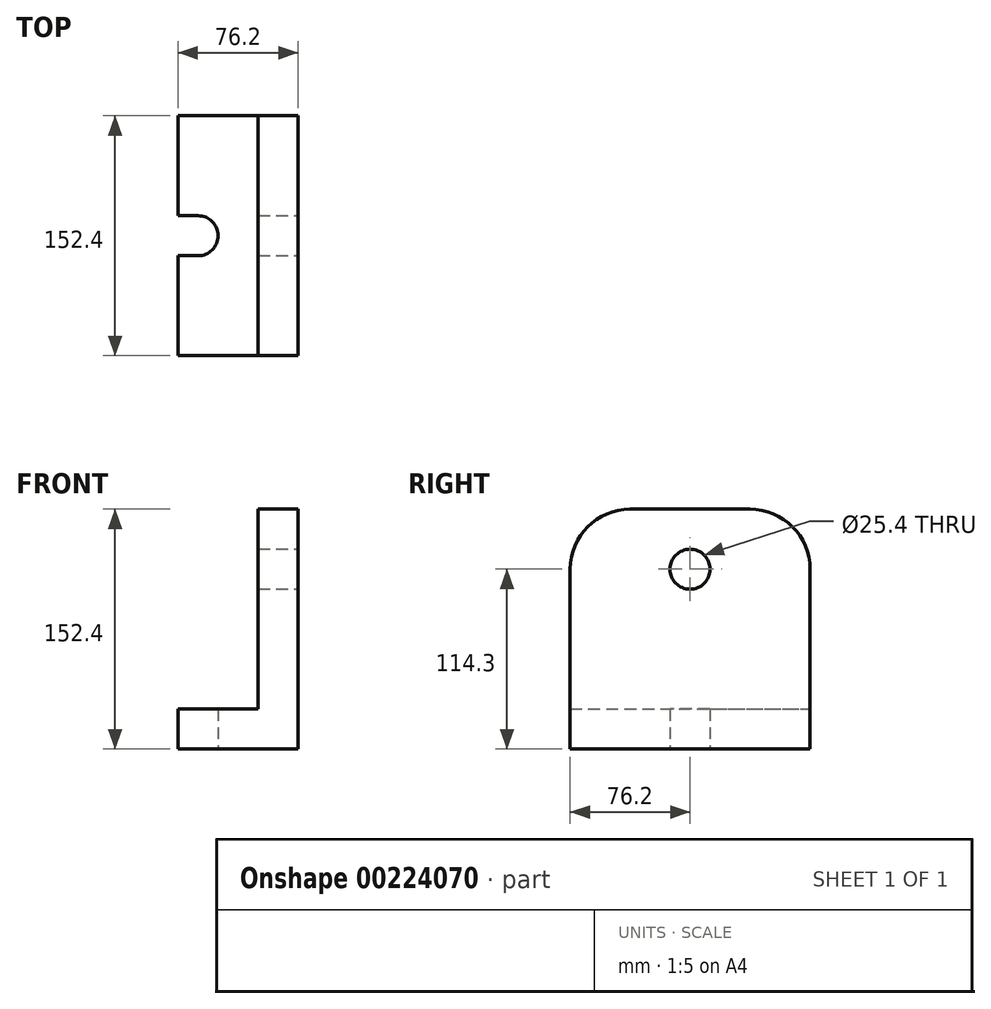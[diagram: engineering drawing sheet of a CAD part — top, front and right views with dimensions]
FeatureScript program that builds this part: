
annotation { "Feature Type Name" : "Feature", "Feature Type Description" : "" }
export const myFeature = defineFeature(function(context is Context, id is Id, definition is map)
    precondition{}
    {
        {
            var Q0;
            Q0=qCreatedBy(makeId("Front.planeOp"),FACE);
            var sketch = newSketch(context, id + "F0", { "sketchPlane" : qUnion([Q0])});
            skLineSegment(sketch, "E0", {"start": v(0, 0) * mm, "end": v(-76.2, 0) * mm});
            skLineSegment(sketch, "E1", {"start": v(0, 0) * mm, "end": v(0, 152.4) * mm});
            skLineSegment(sketch, "E2", {"start": v(0, 152.4) * mm, "end": v(-25.4, 152.4) * mm});
            skLineSegment(sketch, "E3", {"start": v(-25.4, 25.4) * mm, "end": v(-25.4, 152.4) * mm});
            skLineSegment(sketch, "E4", {"start": v(-25.4, 25.4) * mm, "end": v(-76.2, 25.4) * mm});
            skLineSegment(sketch, "E5", {"start": v(-76.2, 25.4) * mm, "end": v(-76.2, 0) * mm});
            skSolve(sketch);
        }
        {
            var Q0;
            Q0=makeQuery(id+"F0.imprint","IMPRINT",FACE,{"disambiguationData":[TD([[makeQuery(id+"F0.imprint","IMPRINT",EDGE,{"derivedFrom":sQuery(id+"F0.wireOp",EDGE,"E0")}),-1.0]])]});
            extrude(context, id + "F1", {"entities" : qUnion([Q0]), "endBound" : BoundingType.SYMMETRIC, "depth" : 152.4 * mm});
        }
        {
            var Q0;
            Q0=makeQuery(id+"F1.opExtrude","SWEPT_FACE",FACE,{"disambiguationData":[OSD([sQuery(id+"F0.wireOp",EDGE,"E1")])]});
            var sketch = newSketch(context, id + "F2", { "sketchPlane" : qUnion([Q0])});
            skPoint(sketch, "E6.endSnap0", {"position": v(0, 152.4) * mm});
            skCircle(sketch, "E7", {"center": v(0, 114.3) * mm, "radius": 12.7 * mm});
            skSolve(sketch);
        }
        {
            var Q0;
            Q0=makeQuery(id+"F2.imprint","IMPRINT",FACE,{"disambiguationData":[TD([[makeQuery(id+"F2.imprint","IMPRINT",EDGE,{"derivedFrom":sQuery(id+"F2.wireOp",EDGE,"E7")}),1.0]])]});
            extrude(context, id + "F3", {"entities" : qUnion([Q0]), "operationType" : NewBodyOperationType.REMOVE, "oppositeDirection" : true, "depth" : 25.4 * mm});
        }
        {
            var Q0;
            Q0=makeQuery(id+"F1.opExtrude","SWEPT_FACE",FACE,{"disambiguationData":[OSD([sQuery(id+"F0.wireOp",EDGE,"E0")])]});
            var sketch = newSketch(context, id + "F4", { "sketchPlane" : qUnion([Q0])});
            skLineSegment(sketch, "E8", {"start": v(-76.2, 0) * mm, "end": v(-76.2, 12.7) * mm});
            skLineSegment(sketch, "E9", {"start": v(-76.2, 0) * mm, "end": v(-76.2, -12.7) * mm});
            skLineSegment(sketch, "E10", {"start": v(-76.2, 12.7) * mm, "end": v(-63.5, 12.7) * mm});
            skLineSegment(sketch, "E11", {"start": v(-76.2, -12.7) * mm, "end": v(-63.5, -12.7) * mm});
            skArc(sketch, "E12", {"start": v(-63.5, 12.7) * mm, "mid": v(-50.8, 0) * mm, "end": v(-63.5, -12.7) * mm});
            skSolve(sketch);
        }
        {
            var Q0;
            Q0 = qSketchRegion(id + "F4", true);
            extrude(context, id + "F5", {"entities" : qUnion([Q0]), "operationType" : NewBodyOperationType.REMOVE, "oppositeDirection" : true, "depth" : 25.4 * mm});
        }
        {
            var Q0;
            Q0=makeQuery(id+"F1.opExtrude","CAP_EDGE",EDGE,{"disambiguationData":[OSD([sQuery(id+"F0.wireOp",EDGE,"E2")])],"isStart":true});
            var Q1;
            Q1=makeQuery(id+"F1.opExtrude","CAP_EDGE",EDGE,{"disambiguationData":[OSD([sQuery(id+"F0.wireOp",EDGE,"E2")])],"isStart":false});
            fillet(context, id + "F6", {"entities" : qUnion([Q0, Q1]), "radius" : 38.1 * mm, "tangentPropagation" : true, "allowEdgeOverflow" : false});
        }
    });
